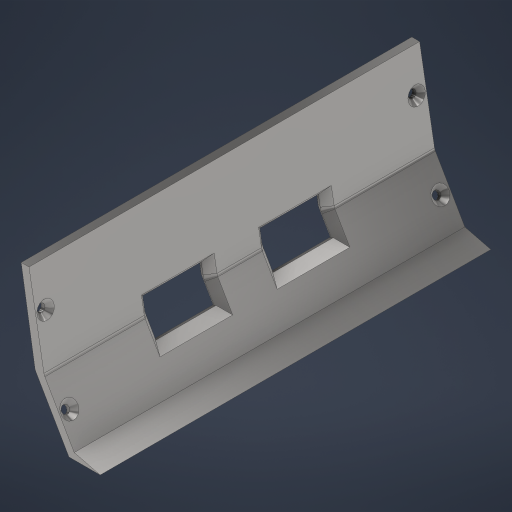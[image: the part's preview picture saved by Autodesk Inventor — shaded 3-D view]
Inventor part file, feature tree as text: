
AUTODESK INVENTOR PART (.ipt)
format: ipt  version: 2024 (Build 280153000, 153)  size: 308,736 bytes
history: native  units: in
note: dims shown in document units (in); Inventor stores cm internally (conversion verified against a paired STEP export)
features: sketch x4, extrude x2, chamfer x2, hole x2
ambient origin geometry x8: Origin, YZ Plane, XZ Plane, XY Plane, X Axis, Y Axis, Z Axis, Center Point
bodies: Solid1 (feature_tree)
feature tree (10):
  extrude  "Extrusion1"  Depth=0.0787in
  extrude  "Extrusion2"  Depth=0.315in
  chamfer  "Chamfer3"  Distance=0.5906in
  sketch  "Sketch7"  dims[d23=0.5906in]
  sketch  "Sketch8"  dims[d24=0.315in d25=0.5906in d26=0.0in d27=0.0in d37=0.6871in d38=0.0787in d39=0.0787in d40=1.378in d41=1.378in d42=0.0709in d43=0.0787in d44=45.0deg d45=0.0787in d46=0.2362in d47=0.1575in d48=0.0787in d49=90.0deg d50=0.315in d51=0.8108in d52=0.0787in d53=0.2362in d54=0.1575in d55=0.0787in d56=90.0deg d57=0.315in d58=0.8108in d59=0.0472in d60=0.0787in d61=45.0deg]
  hole  "Hole2"  [1 undecoded]
  hole  "Hole3"  [1 undecoded]
  chamfer  "Chamfer4"  Distance=0.0787in
  sketch  "Sketch1"  dims[d0=0.315in d1=120.0deg d3=0.0787in]
  sketch  "Sketch6"  dims[d4=3.937in d5=0.0in d22=0.315in]
note: 2 required parameter values undecoded (feature->parameter linkage not recoverable at this tier; creation-order binding heuristic only, values carry confidence <= 0.55)
